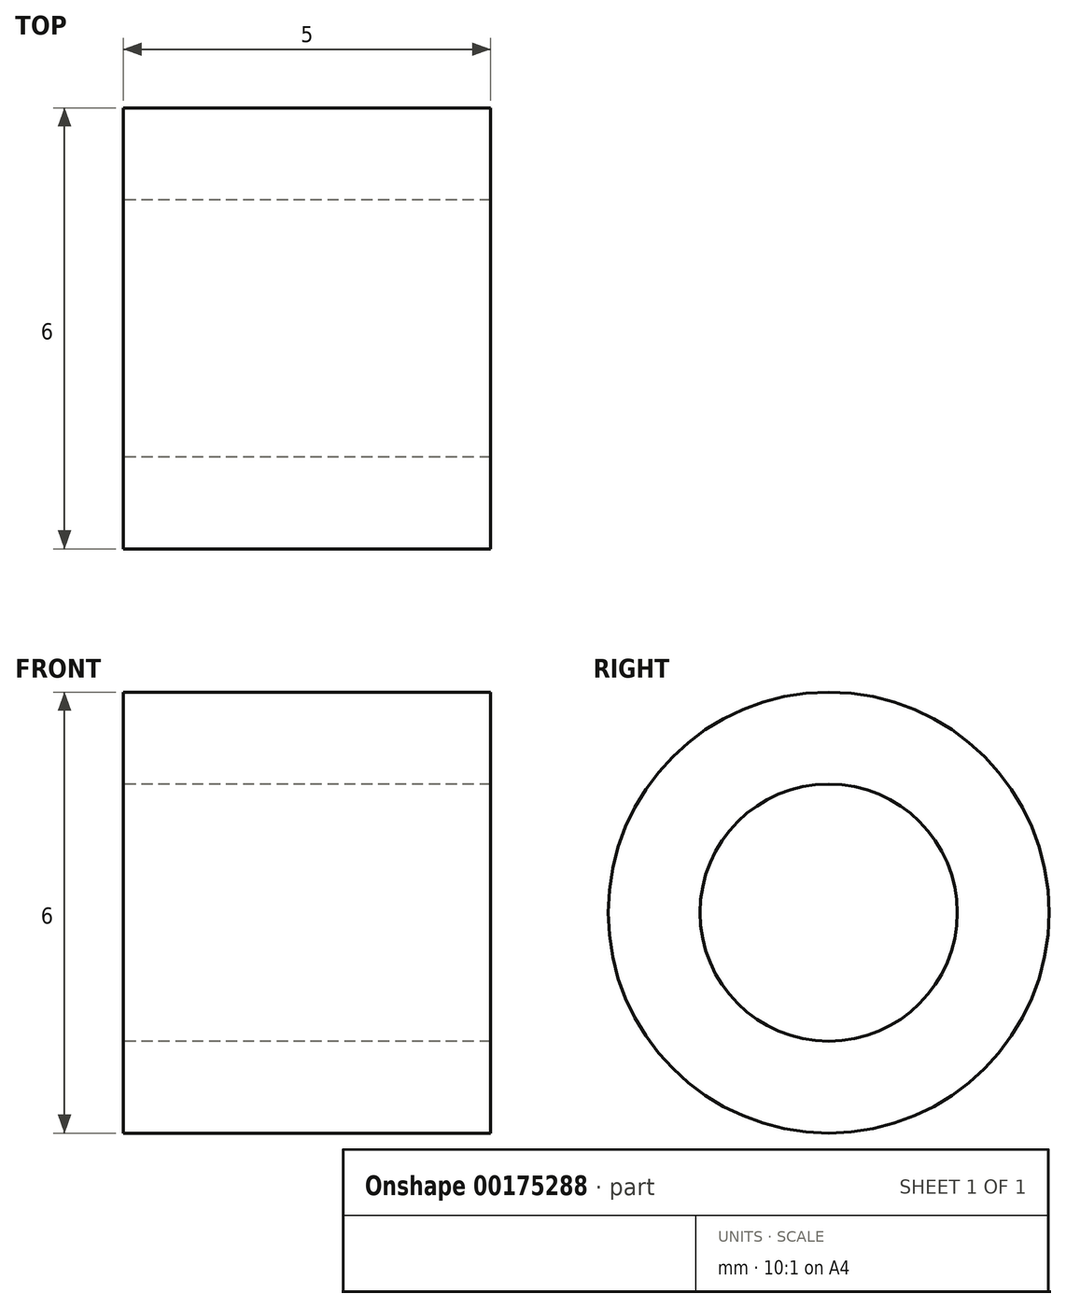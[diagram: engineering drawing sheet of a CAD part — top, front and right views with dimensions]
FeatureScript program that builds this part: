
annotation { "Feature Type Name" : "Feature", "Feature Type Description" : "" }
export const myFeature = defineFeature(function(context is Context, id is Id, definition is map)
    precondition{}
    {
        {
            var Q0;
            Q0=qCreatedBy(makeId("Right.planeOp"),FACE);
            var sketch = newSketch(context, id + "F0", { "sketchPlane" : qUnion([Q0])});
            skCircle(sketch, "E0", {"center": v(0, 0) * mm, "radius": 3 * mm});
            skCircle(sketch, "E1", {"center": v(0, 0) * mm, "radius": 1.75 * mm});
            skSolve(sketch);
        }
        {
            var Q0;
            Q0 = qSketchRegion(id + "F0", true);
            extrude(context, id + "F1", {"entities" : qUnion([Q0]), "depth" : 5 * mm});
        }
    });
